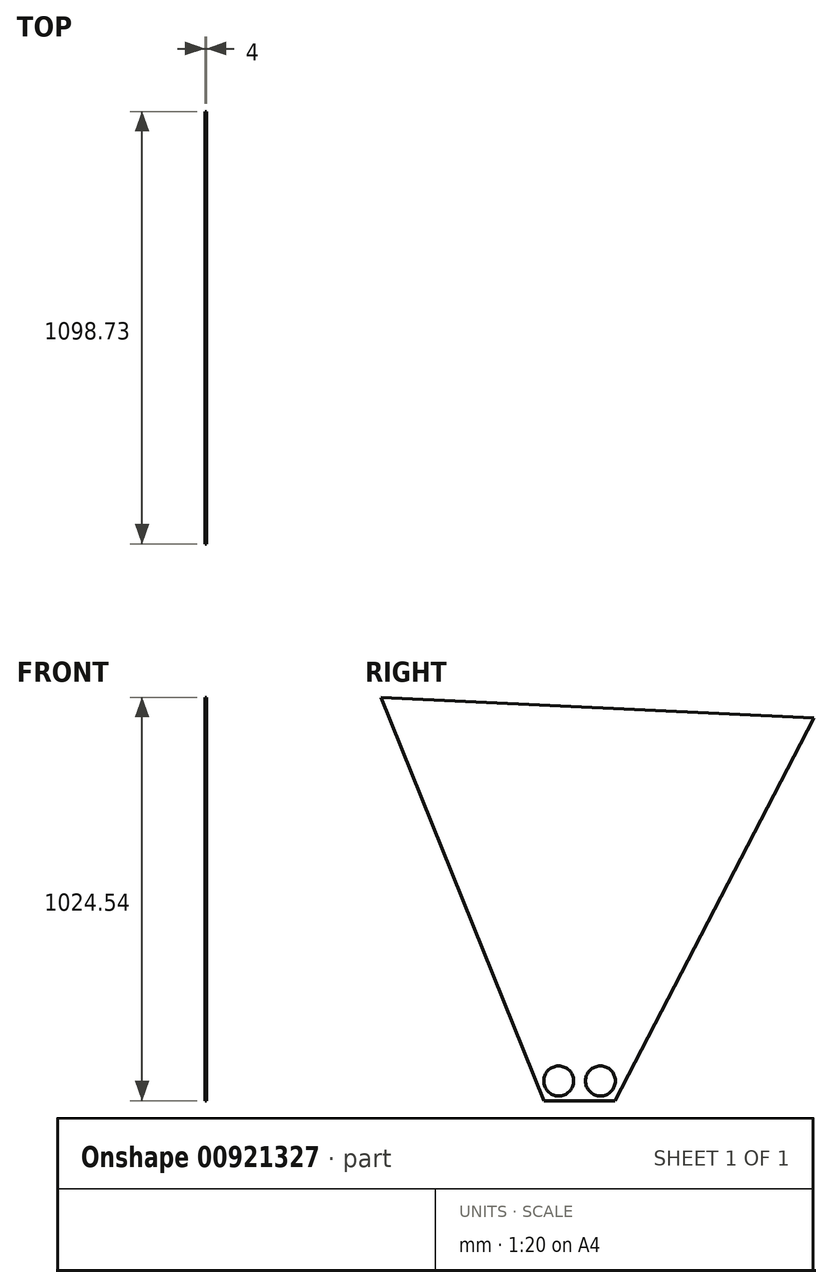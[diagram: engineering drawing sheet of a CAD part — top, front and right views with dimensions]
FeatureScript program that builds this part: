
annotation { "Feature Type Name" : "Feature", "Feature Type Description" : "" }
export const myFeature = defineFeature(function(context is Context, id is Id, definition is map)
    precondition{}
    {
        {
            var Q0;
            Q0=qCreatedBy(makeId("Right.planeOp"),FACE);
            var sketch = newSketch(context, id + "F0", { "sketchPlane" : qUnion([Q0])});
            skLineSegment(sketch, "E0", {"start": v(0, 0) * mm, "end": v(-180, 0) * mm});
            skLineSegment(sketch, "E1", {"start": v(-180, 0) * mm, "end": v(-593.94, 1024.54) * mm});
            skLineSegment(sketch, "E2", {"start": v(-593.94, 1024.54) * mm, "end": v(504.8, 971.7) * mm});
            skLineSegment(sketch, "E3", {"start": v(504.8, 971.7) * mm, "end": v(0, 0) * mm});
            skCircle(sketch, "E4", {"center": v(-143, 50) * mm, "radius": 38 * mm});
            skCircle(sketch, "E5", {"center": v(-37, 50) * mm, "radius": 38 * mm});
            skLineSegment(sketch, "E6", {"start": v(-143, 50) * mm, "end": v(-37, 50) * mm, "construction": true});
            skLineSegment(sketch, "E7", {"start": v(-90, 50) * mm, "end": v(-90, 0) * mm, "construction": true});
            skSolve(sketch);
        }
        {
            var Q0;
            Q0 = qSketchRegion(id + "F0", true);
            extrude(context, id + "F1", {"entities" : qUnion([Q0]), "depth" : 4 * mm, "offsetDistance" : 25 * mm});
        }
    });
